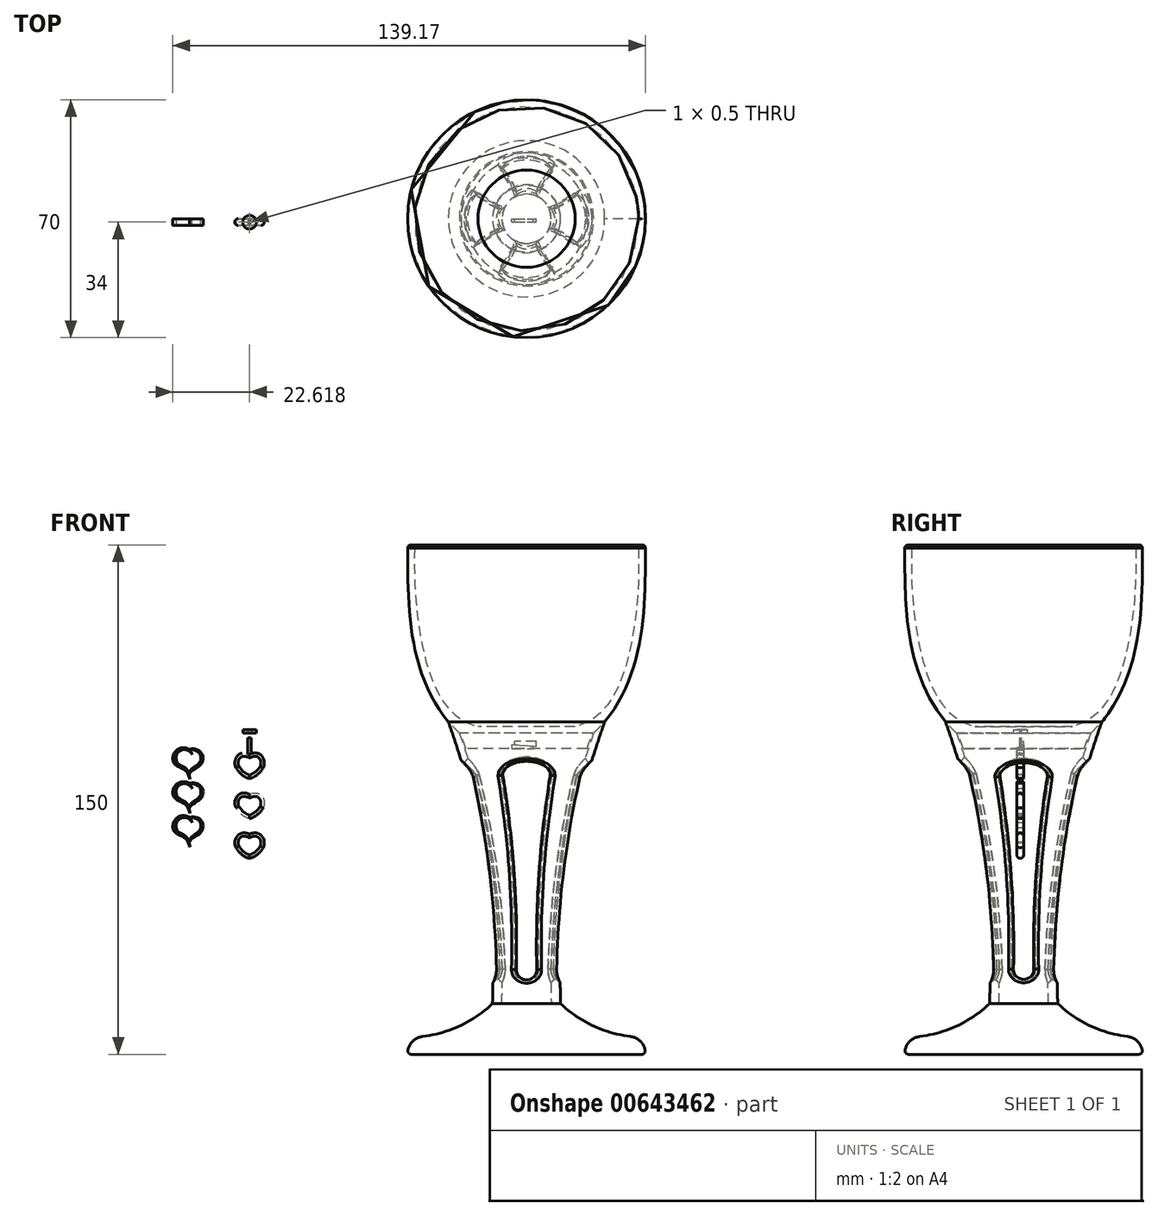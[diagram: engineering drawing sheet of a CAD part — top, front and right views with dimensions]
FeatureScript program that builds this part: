
annotation { "Feature Type Name" : "Feature", "Feature Type Description" : "" }
export const myFeature = defineFeature(function(context is Context, id is Id, definition is map)
    precondition{}
    {
        {
            var Q0;
            Q0=qCreatedBy(makeId("Front.planeOp"),FACE);
            var sketch = newSketch(context, id + "F0", { "sketchPlane" : qUnion([Q0])});
            skLineSegment(sketch, "E0", {"start": v(0, 130.44) * mm, "end": v(0, -127.8) * mm, "construction": true});
            skLineSegment(sketch, "E1", {"start": v(-47.74, 60) * mm, "end": v(50.5, 60) * mm, "construction": true});
            skLineSegment(sketch, "E2", {"start": v(-35, 85.65) * mm, "end": v(-35, -93.9) * mm, "construction": true});
            skFitSpline(sketch, "E3", {"points": [v(-33, 60) * mm, v(-33, 52.2) * mm, v(-31.65, 35.66) * mm, v(-19.66, 8.83) * mm, v(0, 5.37) * mm], "startDerivative": vector(0.17, -46.98) * mm, "endDerivative": vector(45.68, -2.23) * mm});
            skLineSegment(sketch, "E4", {"start": v(-35, 60) * mm, "end": v(-33, 60) * mm});
            skLineSegment(sketch, "E5", {"start": v(0, 5.37) * mm, "end": v(0, 0) * mm});
            skLineSegment(sketch, "E6.left", {"start": v(-35, -90) * mm, "end": v(-34.96, -85) * mm});
            skLineSegment(sketch, "E7", {"start": v(0, -75.08) * mm, "end": v(0, -90) * mm});
            skLineSegment(sketch, "E8", {"start": v(-35, -90) * mm, "end": v(0, -90) * mm});
            skLineSegment(sketch, "E9", {"start": v(-10.04, -75.08) * mm, "end": v(0, -75.08) * mm});
            skArc(sketch, "E10", {"start": v(-34.96, -85) * mm, "mid": v(-21.54, -82.44) * mm, "end": v(-10.04, -75.08) * mm});
            skArc(sketch, "E11", {"start": v(-10.04, -75.08) * mm, "mid": v(-12.53, -33) * mm, "end": v(-23, 7.81) * mm});
            skArc(sketch, "E12", {"start": v(-7.28, -75.08) * mm, "mid": v(-9.85, -34.66) * mm, "end": v(-19.78, 4.6) * mm});
            skLineSegment(sketch, "E13", {"start": v(0, -1.5) * mm, "end": v(0, -2.5) * mm});
            skLineSegment(sketch, "E14", {"start": v(61.71, 9.52) * mm, "end": v(61.71, -82.4) * mm, "construction": true});
            skLineSegment(sketch, "E15", {"start": v(56.71, 9.98) * mm, "end": v(56.71, -82.7) * mm, "construction": true});
            skLineSegment(sketch, "E16", {"start": v(66.71, 9.98) * mm, "end": v(66.71, -82.7) * mm, "construction": true});
            skCircle(sketch, "E17", {"center": v(61.71, -11.74) * mm, "radius": 5 * mm, "construction": true});
            skLineSegment(sketch, "E18", {"start": v(68.56, -11.74) * mm, "end": v(55.91, -11.74) * mm, "construction": true});
            skFitSpline(sketch, "E19", {"points": [v(56.71, -11.74) * mm, v(57.38, -9.69) * mm, v(58.5, -8.73) * mm, v(59.57, -8.36) * mm, v(60.79, -8.44) * mm, v(61.56, -8.81) * mm, v(62.29, -10.09) * mm], "startDerivative": vector(0, 9.46) * mm, "endDerivative": vector(1.96, -9.79) * mm});
            skFitSpline(sketch, "E20", {"points": [v(62.29, -10.09) * mm, v(61.51, -9.22) * mm, v(60.19, -8.85) * mm, v(58.82, -9.37) * mm, v(57.98, -10.52) * mm, v(57.77, -12.56) * mm, v(58.79, -14.06) * mm, v(60.05, -14.58) * mm, v(61.03, -15.06) * mm, v(61.7, -15.92) * mm, v(61.71, -16.74) * mm], "startDerivative": vector(-9, 11.38) * mm, "endDerivative": vector(1.36, -12.04) * mm});
            skFitSpline(sketch, "E21", {"points": [v(56.71, -11.74) * mm, v(57, -13.39) * mm, v(57.72, -14.57) * mm, v(58.7, -15.24) * mm, v(59.87, -15.43) * mm, v(60.66, -15.55) * mm, v(61.35, -16) * mm, v(61.71, -16.74) * mm], "startDerivative": vector(0.44, -8.79) * mm, "endDerivative": vector(1.87, -8.34) * mm});
            skFitSpline(sketch, "E22", {"points": [v(61.56, -8.81) * mm, v(62.83, -8.64) * mm, v(64.34, -9.22) * mm, v(65.25, -10.62) * mm, v(64.91, -12.42) * mm, v(63.93, -13.45) * mm, v(62.9, -14.12) * mm, v(62.02, -14.74) * mm, v(61.51, -15.54) * mm], "startDerivative": vector(10.18, 4.63) * mm, "endDerivative": vector(-2.51, -8.3) * mm});
            skFitSpline(sketch, "E23", {"points": [v(61.71, -8.96) * mm, v(62.62, -8.91) * mm, v(63.32, -9.16) * mm, v(63.92, -9.5) * mm, v(64.36, -10.01) * mm, v(64.59, -10.6) * mm, v(64.63, -11.56) * mm, v(64.27, -12.27) * mm, v(63.84, -12.76) * mm, v(63.38, -13.1) * mm, v(62.85, -13.48) * mm, v(62.33, -13.88) * mm, v(61.9, -14.3) * mm, v(61.53, -14.86) * mm, v(61.4, -15.4) * mm], "startDerivative": vector(9.48, 3.87) * mm, "endDerivative": vector(2.37, 8.87) * mm});
            skLineSegment(sketch, "E24", {"start": v(0, 0) * mm, "end": v(-17.82, 0) * mm});
            skLineSegment(sketch, "E25", {"start": v(-23, 7.81) * mm, "end": v(-19.78, 4.6) * mm});
            skFitSpline(sketch, "E26", {"points": [v(-35, 60) * mm, v(-23, 7.81) * mm], "startDerivative": vector(0, -56.24) * mm, "endDerivative": vector(36, -44.82) * mm});
            skLineSegment(sketch, "E27", {"start": v(-17.82, 0) * mm, "end": v(-19.37, 4.58) * mm});
            skLineSegment(sketch, "E28", {"start": v(-19.37, 4.58) * mm, "end": v(-19.78, 4.6) * mm});
            skLineSegment(sketch, "E29", {"start": v(-14.32, 6.5) * mm, "end": v(0, 6.5) * mm});
            skLineSegment(sketch, "E30", {"start": v(0, 6.5) * mm, "end": v(0, 5.37) * mm});
            skSolve(sketch);
        }
        {
            var Q0;
            Q0=makeQuery(id+"F0.imprint","IMPRINT",FACE,{"disambiguationData":[TD([[makeQuery(id+"F0.imprint","IMPRINT",EDGE,{"derivedFrom":sQuery(id+"F0.wireOp",EDGE,"E6.left")}),-1.0]])]});
            var Q1;
            {var subQ0=sQuery(id+"F0.wireOp",EDGE,"E11");Q1=makeQuery(id+"F0.imprint","IMPRINT",FACE,{"disambiguationData":[TD([[makeQuery(id+"F0.imprint","IMPRINT",EDGE,{"derivedFrom":subQ0}),-1.0]])]});}
            var Q2;
            Q2=sQuery(id+"F0.wireOp",EDGE,"E0");
            revolve(context, id + "F1", {"entities" : qUnion([Q0, Q1]), "axis" : qUnion([Q2]), "revolveType" : RevolveType.FULL});
        }
        {
            var Q0;
            Q0=makeQuery(id+"F0.imprint","IMPRINT",FACE,{"disambiguationData":[TD([[makeQuery(id+"F0.imprint","IMPRINT",EDGE,{"derivedFrom":sQuery(id+"F0.wireOp",EDGE,"E3")}),-1.0]])]});
            var Q1;
            {var subQ2=sQuery(id+"F0.wireOp",EDGE,"E29");Q1=makeQuery(id+"F0.imprint","IMPRINT",FACE,{"disambiguationData":[TD([[makeQuery(id+"F0.imprint","IMPRINT",EDGE,{"derivedFrom":subQ2}),-1.0]])]});}
            var Q2;
            Q2=sQuery(id+"F0.wireOp",EDGE,"E3");
            var Q3;
            Q3=sQuery(id+"F0.wireOp",EDGE,"58f8bd6e-e700-4917-940a-16b648b99986");
            var Q4;
            Q4=sQuery(id+"F0.wireOp",EDGE,"E4");
            var Q5;
            Q5=sQuery(id+"F0.wireOp",EDGE,"E0");
            revolve(context, id + "F2", {"entities" : qUnion([Q0, Q1]), "surfaceEntities" : qUnion([Q2, Q3, Q4]), "axis" : qUnion([Q5]), "revolveType" : RevolveType.FULL});
        }
        {
            var Q0;
            Q0=qCreatedBy(makeId("Front.planeOp"),FACE);
            var sketch = newSketch(context, id + "F3", { "sketchPlane" : qUnion([Q0])});
            skLineSegment(sketch, "E31", {"start": v(0, 0) * mm, "end": v(0, -71.87) * mm, "construction": true});
            skLineSegment(sketch, "E32", {"start": v(-19.04, -7.62) * mm, "end": v(33.65, -7.62) * mm, "construction": true});
            skLineSegment(sketch, "E33", {"start": v(-18.09, -65.08) * mm, "end": v(18.02, -65.08) * mm, "construction": true});
            skArc(sketch, "E34", {"start": v(-3, -65.08) * mm, "mid": v(-3.68, -36.26) * mm, "end": v(-7, -7.62) * mm});
            skArc(sketch, "E35", {"start": v(-3, -65.08) * mm, "mid": v(0, -68.08) * mm, "end": v(3, -65.08) * mm});
            skPoint(sketch, "E35.centerSnap0", {"position": v(-0.03, -65.08) * mm});
            skLineSegment(sketch, "E36", {"start": v(-7, -7.62) * mm, "end": v(0, -7.62) * mm});
            skLineSegment(sketch, "E37", {"start": v(0, -68.08) * mm, "end": v(0, -7.62) * mm});
            skArc(sketch, "E38.MirrorCS", {"start": v(3, -65.08) * mm, "mid": v(3.68, -36.26) * mm, "end": v(7, -7.62) * mm});
            skEllipse(sketch, "E39", {"center": v(0, -7.62) * mm, "majorRadius": 7 * mm, "minorRadius": 3.89 * mm, "majorAxis": v(-1, 0)});
            skSolve(sketch);
        }
        {
            var Q0;
            {var subQ6=sQuery(id+"F3.wireOp",EDGE,"E36");Q0=makeQuery(id+"F3.imprint","IMPRINT",FACE,{"disambiguationData":[TD([[makeQuery(id+"F3.imprint","IMPRINT",EDGE,{"derivedFrom":subQ6}),1.0]])]});}
            var Q1;
            {var subQ1=sQuery(id+"F3.wireOp",EDGE,"E36");Q1=makeQuery(id+"F3.imprint","IMPRINT",FACE,{"disambiguationData":[TD([[makeQuery(id+"F3.imprint","IMPRINT",EDGE,{"derivedFrom":subQ1}),-1.0]])]});}
            var Q2;
            {var subQ0=sQuery(id+"F3.wireOp",EDGE,"E35");var subQ1=sQuery(id+"F3.wireOp",EDGE,"E34");var subQ2=makeQuery(id+"F3.imprint","INTERSECT",VERTEX,{"derivedFrom":[subQ1,subQ0]});Q2=makeQuery(id+"F3.imprint","IMPRINT",FACE,{"disambiguationData":[TD([[makeQuery(id+"F3.imprint","IMPRINT",EDGE,{"disambiguationData":[TD([[subQ2,-1.0]])],"derivedFrom":subQ1}),-1.0]])]});}
            var Q3;
            {var subQ0=sQuery(id+"F3.wireOp",EDGE,"E38.MirrorCS");var subQ1=sQuery(id+"F3.wireOp",EDGE,"E35");var subQ2=makeQuery(id+"F3.imprint","INTERSECT",VERTEX,{"derivedFrom":[subQ1,subQ0]});Q3=makeQuery(id+"F3.imprint","IMPRINT",FACE,{"disambiguationData":[TD([[makeQuery(id+"F3.imprint","IMPRINT",EDGE,{"disambiguationData":[TD([[subQ2,1.0]])],"derivedFrom":subQ1}),1.0]])]});}
            extrude(context, id + "F4", {"entities" : qUnion([Q0, Q1, Q2, Q3]), "depth" : 50 * mm, "offsetDistance" : 25 * mm});
        }
        {
            var Q0;
            Q0=makeQuery(id+"F4.opExtrude","SWEPT_BODY",BODY,{"disambiguationData":[OSD([sQuery(id+"F3.wireOp",EDGE,"E34"),sQuery(id+"F3.wireOp",EDGE,"E35"),sQuery(id+"F3.wireOp",EDGE,"E38.MirrorCS"),sQuery(id+"F3.wireOp",EDGE,"E39")])]});
            transform(context, id + "F5", {"entities" : qUnion([Q0]), "transformType" : TransformType.TRANSLATION_3D, "dx" : 0 * mm, "dy" : 25 * mm, "dz" : 0 * mm, "makeCopy" : false});
        }
        {
            var Q0;
            Q0=makeQuery(id+"F4.opExtrude","SWEPT_BODY",BODY,{"disambiguationData":[OSD([sQuery(id+"F3.wireOp",EDGE,"E34"),sQuery(id+"F3.wireOp",EDGE,"E35"),sQuery(id+"F3.wireOp",EDGE,"E38.MirrorCS"),sQuery(id+"F3.wireOp",EDGE,"E39")])]});
            var Q1;
            Q1=makeQuery(id+"F1.opRevolve","SWEPT_BODY",BODY,{"disambiguationData":[OSD([sQuery(id+"F0.wireOp",EDGE,"58f8bd6e-e700-4917-940a-16b648b99986"),sQuery(id+"F0.wireOp",EDGE,"E3"),sQuery(id+"F0.wireOp",EDGE,"E4"),sQuery(id+"F0.wireOp",EDGE,"E5"),sQuery(id+"F0.wireOp",EDGE,"E6.left"),sQuery(id+"F0.wireOp",EDGE,"E7"),sQuery(id+"F0.wireOp",EDGE,"E8"),sQuery(id+"F0.wireOp",EDGE,"E9"),sQuery(id+"F0.wireOp",EDGE,"E10"),sQuery(id+"F0.wireOp",EDGE,"E11"),sQuery(id+"F0.wireOp",EDGE,"E12")])]});
            booleanBodies(context, id + "F6", {"operationType" : BooleanOperationType.SUBTRACTION, "tools" : qUnion([Q0]), "targets" : qUnion([Q1])});
        }
        {
            var Q0;
            Q0=qCreatedBy(makeId("Right.planeOp"),FACE);
            var sketch = newSketch(context, id + "F7", { "sketchPlane" : qUnion([Q0])});
            skLineSegment(sketch, "E40", {"start": v(0, -0.03) * mm, "end": v(0, -71.9) * mm, "construction": true});
            skLineSegment(sketch, "E41", {"start": v(-16.9, -8.05) * mm, "end": v(35.8, -8.05) * mm, "construction": true});
            skLineSegment(sketch, "E42", {"start": v(-14.28, -64.93) * mm, "end": v(21.82, -64.93) * mm, "construction": true});
            skArc(sketch, "E43", {"start": v(-3, -64.93) * mm, "mid": v(-3.7, -36.4) * mm, "end": v(-7, -8.05) * mm});
            skArc(sketch, "E44", {"start": v(-3, -64.93) * mm, "mid": v(0, -67.93) * mm, "end": v(3, -64.93) * mm});
            skPoint(sketch, "E44.centerSnap0", {"position": v(3.77, -64.93) * mm});
            skLineSegment(sketch, "E45", {"start": v(-7, -8.05) * mm, "end": v(0, -8.05) * mm});
            skLineSegment(sketch, "E46", {"start": v(0, -67.93) * mm, "end": v(0, -8.05) * mm});
            skArc(sketch, "E47.MirrorCS", {"start": v(3, -64.93) * mm, "mid": v(3.7, -36.4) * mm, "end": v(7, -8.05) * mm});
            skEllipse(sketch, "E48", {"center": v(0, -8.05) * mm, "majorRadius": 7 * mm, "minorRadius": 3.89 * mm, "majorAxis": v(-1, 0)});
            skSolve(sketch);
        }
        {
            var Q0;
            {var subQ6=sQuery(id+"F7.wireOp",EDGE,"E45");Q0=makeQuery(id+"F7.imprint","IMPRINT",FACE,{"disambiguationData":[TD([[makeQuery(id+"F7.imprint","IMPRINT",EDGE,{"derivedFrom":subQ6}),1.0]])]});}
            var Q1;
            {var subQ1=sQuery(id+"F7.wireOp",EDGE,"E45");Q1=makeQuery(id+"F7.imprint","IMPRINT",FACE,{"disambiguationData":[TD([[makeQuery(id+"F7.imprint","IMPRINT",EDGE,{"derivedFrom":subQ1}),-1.0]])]});}
            var Q2;
            {var subQ0=sQuery(id+"F7.wireOp",EDGE,"E44");var subQ1=sQuery(id+"F7.wireOp",EDGE,"E43");var subQ2=makeQuery(id+"F7.imprint","INTERSECT",VERTEX,{"derivedFrom":[subQ1,subQ0]});Q2=makeQuery(id+"F7.imprint","IMPRINT",FACE,{"disambiguationData":[TD([[makeQuery(id+"F7.imprint","IMPRINT",EDGE,{"disambiguationData":[TD([[subQ2,-1.0]])],"derivedFrom":subQ1}),-1.0]])]});}
            var Q3;
            {var subQ0=sQuery(id+"F7.wireOp",EDGE,"E47.MirrorCS");var subQ1=sQuery(id+"F7.wireOp",EDGE,"E44");var subQ2=makeQuery(id+"F7.imprint","INTERSECT",VERTEX,{"derivedFrom":[subQ1,subQ0]});Q3=makeQuery(id+"F7.imprint","IMPRINT",FACE,{"disambiguationData":[TD([[makeQuery(id+"F7.imprint","IMPRINT",EDGE,{"disambiguationData":[TD([[subQ2,1.0]])],"derivedFrom":subQ1}),1.0]])]});}
            extrude(context, id + "F8", {"entities" : qUnion([Q0, Q1, Q2, Q3]), "depth" : 50 * mm, "offsetDistance" : 25 * mm});
        }
        {
            var Q0;
            Q0=makeQuery(id+"F8.opExtrude","SWEPT_BODY",BODY,{"disambiguationData":[OSD([sQuery(id+"F7.wireOp",EDGE,"E43"),sQuery(id+"F7.wireOp",EDGE,"E44"),sQuery(id+"F7.wireOp",EDGE,"E47.MirrorCS"),sQuery(id+"F7.wireOp",EDGE,"E48")])]});
            transform(context, id + "F9", {"entities" : qUnion([Q0]), "transformType" : TransformType.TRANSLATION_3D, "dx" : -25 * mm, "dy" : 0 * mm, "dz" : 0 * mm, "makeCopy" : false});
        }
        {
            var Q0;
            Q0=makeQuery(id+"F8.opExtrude","SWEPT_BODY",BODY,{"disambiguationData":[OSD([sQuery(id+"F7.wireOp",EDGE,"E43"),sQuery(id+"F7.wireOp",EDGE,"E44"),sQuery(id+"F7.wireOp",EDGE,"E47.MirrorCS"),sQuery(id+"F7.wireOp",EDGE,"E48")])]});
            var Q1;
            Q1=makeQuery(id+"F1.opRevolve","SWEPT_BODY",BODY,{"disambiguationData":[OSD([sQuery(id+"F0.wireOp",EDGE,"58f8bd6e-e700-4917-940a-16b648b99986"),sQuery(id+"F0.wireOp",EDGE,"E6.left"),sQuery(id+"F0.wireOp",EDGE,"E7"),sQuery(id+"F0.wireOp",EDGE,"E8"),sQuery(id+"F0.wireOp",EDGE,"E9"),sQuery(id+"F0.wireOp",EDGE,"E10"),sQuery(id+"F0.wireOp",EDGE,"E11"),sQuery(id+"F0.wireOp",EDGE,"E12")])]});
            booleanBodies(context, id + "F10", {"operationType" : BooleanOperationType.SUBTRACTION, "tools" : qUnion([Q0]), "targets" : qUnion([Q1])});
        }
        {
            var Q0;
            Q0=makeQuery(id+"F1.opRevolve","SWEPT_EDGE",EDGE,{"disambiguationData":[OSD([sQuery(id+"F0.wireOp",EDGE,"E6.left"),sQuery(id+"F0.wireOp",EDGE,"E10")])]});
            fillet(context, id + "F11", {"entities" : qUnion([Q0]), "radius" : 5 * mm, "tangentPropagation" : true, "allowEdgeOverflow" : false});
        }
        {
            var Q0;
            Q0=makeQuery(id+"F1.opRevolve","SWEPT_EDGE",EDGE,{"disambiguationData":[OSD([sQuery(id+"F0.wireOp",EDGE,"E6.left"),sQuery(id+"F0.wireOp",EDGE,"E8")])]});
            fillet(context, id + "F12", {"entities" : qUnion([Q0]), "radius" : 1 * mm, "tangentPropagation" : true, "allowEdgeOverflow" : false});
        }
        {
            var Q0;
            Q0=makeQuery(id+"F10.opBoolean","INTERSECT",EDGE,{"disambiguationData":[OD(1.0)],"derivedFrom":[makeQuery(id+"F1.opRevolve","SWEPT_FACE",FACE,{"disambiguationData":[OSD([sQuery(id+"F0.wireOp",EDGE,"E11")])]}),makeQuery(id+"F8.opExtrude","SWEPT_FACE",FACE,{"disambiguationData":[OSD([sQuery(id+"F7.wireOp",EDGE,"E47.MirrorCS")])]})]});
            var Q1;
            Q1=makeQuery(id+"F10.opBoolean","INTERSECT",EDGE,{"disambiguationData":[OD(1.0)],"derivedFrom":[makeQuery(id+"F1.opRevolve","SWEPT_FACE",FACE,{"disambiguationData":[OSD([sQuery(id+"F0.wireOp",EDGE,"E11")])]}),makeQuery(id+"F8.opExtrude","SWEPT_FACE",FACE,{"disambiguationData":[OSD([sQuery(id+"F7.wireOp",EDGE,"E48")])]})]});
            var Q2;
            Q2=makeQuery(id+"F10.opBoolean","INTERSECT",EDGE,{"disambiguationData":[OD(1.0)],"derivedFrom":[makeQuery(id+"F1.opRevolve","SWEPT_FACE",FACE,{"disambiguationData":[OSD([sQuery(id+"F0.wireOp",EDGE,"E11")])]}),makeQuery(id+"F8.opExtrude","SWEPT_FACE",FACE,{"disambiguationData":[OSD([sQuery(id+"F7.wireOp",EDGE,"E43")])]})]});
            var Q3;
            Q3=makeQuery(id+"F6.opBoolean","INTERSECT",EDGE,{"disambiguationData":[OD(1.0)],"derivedFrom":[makeQuery(id+"F1.opRevolve","SWEPT_FACE",FACE,{"disambiguationData":[OSD([sQuery(id+"F0.wireOp",EDGE,"E11")])]}),makeQuery(id+"F4.opExtrude","SWEPT_FACE",FACE,{"disambiguationData":[OSD([sQuery(id+"F3.wireOp",EDGE,"E34")])]})]});
            var Q4;
            Q4=makeQuery(id+"F6.opBoolean","INTERSECT",EDGE,{"disambiguationData":[OD(1.0)],"derivedFrom":[makeQuery(id+"F1.opRevolve","SWEPT_FACE",FACE,{"disambiguationData":[OSD([sQuery(id+"F0.wireOp",EDGE,"E11")])]}),makeQuery(id+"F4.opExtrude","SWEPT_FACE",FACE,{"disambiguationData":[OSD([sQuery(id+"F3.wireOp",EDGE,"E35")])]})]});
            var Q5;
            Q5=makeQuery(id+"F6.opBoolean","INTERSECT",EDGE,{"disambiguationData":[OD(1.0)],"derivedFrom":[makeQuery(id+"F1.opRevolve","SWEPT_FACE",FACE,{"disambiguationData":[OSD([sQuery(id+"F0.wireOp",EDGE,"E11")])]}),makeQuery(id+"F4.opExtrude","SWEPT_FACE",FACE,{"disambiguationData":[OSD([sQuery(id+"F3.wireOp",EDGE,"E38.MirrorCS")])]})]});
            var Q6;
            Q6=makeQuery(id+"F6.opBoolean","INTERSECT",EDGE,{"disambiguationData":[OD(1.0)],"derivedFrom":[makeQuery(id+"F1.opRevolve","SWEPT_FACE",FACE,{"disambiguationData":[OSD([sQuery(id+"F0.wireOp",EDGE,"E11")])]}),makeQuery(id+"F4.opExtrude","SWEPT_FACE",FACE,{"disambiguationData":[OSD([sQuery(id+"F3.wireOp",EDGE,"E39")])]})]});
            var Q7;
            Q7=makeQuery(id+"F6.opBoolean","INTERSECT",EDGE,{"disambiguationData":[OD(1.0)],"derivedFrom":[makeQuery(id+"F1.opRevolve","SWEPT_FACE",FACE,{"disambiguationData":[OSD([sQuery(id+"F0.wireOp",EDGE,"E12")])]}),makeQuery(id+"F4.opExtrude","SWEPT_FACE",FACE,{"disambiguationData":[OSD([sQuery(id+"F3.wireOp",EDGE,"E39")])]})]});
            var Q8;
            Q8=makeQuery(id+"F6.opBoolean","INTERSECT",EDGE,{"disambiguationData":[OD(1.0)],"derivedFrom":[makeQuery(id+"F1.opRevolve","SWEPT_FACE",FACE,{"disambiguationData":[OSD([sQuery(id+"F0.wireOp",EDGE,"E12")])]}),makeQuery(id+"F4.opExtrude","SWEPT_FACE",FACE,{"disambiguationData":[OSD([sQuery(id+"F3.wireOp",EDGE,"E34")])]})]});
            var Q9;
            Q9=makeQuery(id+"F6.opBoolean","INTERSECT",EDGE,{"disambiguationData":[OD(1.0)],"derivedFrom":[makeQuery(id+"F1.opRevolve","SWEPT_FACE",FACE,{"disambiguationData":[OSD([sQuery(id+"F0.wireOp",EDGE,"E12")])]}),makeQuery(id+"F4.opExtrude","SWEPT_FACE",FACE,{"disambiguationData":[OSD([sQuery(id+"F3.wireOp",EDGE,"E35")])]})]});
            var Q10;
            Q10=makeQuery(id+"F6.opBoolean","INTERSECT",EDGE,{"disambiguationData":[OD(1.0)],"derivedFrom":[makeQuery(id+"F1.opRevolve","SWEPT_FACE",FACE,{"disambiguationData":[OSD([sQuery(id+"F0.wireOp",EDGE,"E12")])]}),makeQuery(id+"F4.opExtrude","SWEPT_FACE",FACE,{"disambiguationData":[OSD([sQuery(id+"F3.wireOp",EDGE,"E38.MirrorCS")])]})]});
            var Q11;
            Q11=makeQuery(id+"F10.opBoolean","INTERSECT",EDGE,{"disambiguationData":[OD(1.0)],"derivedFrom":[makeQuery(id+"F1.opRevolve","SWEPT_FACE",FACE,{"disambiguationData":[OSD([sQuery(id+"F0.wireOp",EDGE,"E12")])]}),makeQuery(id+"F8.opExtrude","SWEPT_FACE",FACE,{"disambiguationData":[OSD([sQuery(id+"F7.wireOp",EDGE,"E43")])]})]});
            var Q12;
            Q12=makeQuery(id+"F10.opBoolean","INTERSECT",EDGE,{"disambiguationData":[OD(1.0)],"derivedFrom":[makeQuery(id+"F1.opRevolve","SWEPT_FACE",FACE,{"disambiguationData":[OSD([sQuery(id+"F0.wireOp",EDGE,"E12")])]}),makeQuery(id+"F8.opExtrude","SWEPT_FACE",FACE,{"disambiguationData":[OSD([sQuery(id+"F7.wireOp",EDGE,"E44")])]})]});
            var Q13;
            Q13=makeQuery(id+"F10.opBoolean","INTERSECT",EDGE,{"disambiguationData":[OD(1.0)],"derivedFrom":[makeQuery(id+"F1.opRevolve","SWEPT_FACE",FACE,{"disambiguationData":[OSD([sQuery(id+"F0.wireOp",EDGE,"E12")])]}),makeQuery(id+"F8.opExtrude","SWEPT_FACE",FACE,{"disambiguationData":[OSD([sQuery(id+"F7.wireOp",EDGE,"E47.MirrorCS")])]})]});
            var Q14;
            Q14=makeQuery(id+"F10.opBoolean","INTERSECT",EDGE,{"disambiguationData":[OD(1.0)],"derivedFrom":[makeQuery(id+"F1.opRevolve","SWEPT_FACE",FACE,{"disambiguationData":[OSD([sQuery(id+"F0.wireOp",EDGE,"E12")])]}),makeQuery(id+"F8.opExtrude","SWEPT_FACE",FACE,{"disambiguationData":[OSD([sQuery(id+"F7.wireOp",EDGE,"E48")])]})]});
            var Q15;
            Q15=makeQuery(id+"F6.opBoolean","INTERSECT",EDGE,{"disambiguationData":[OD(0.0)],"derivedFrom":[makeQuery(id+"F1.opRevolve","SWEPT_FACE",FACE,{"disambiguationData":[OSD([sQuery(id+"F0.wireOp",EDGE,"E12")])]}),makeQuery(id+"F4.opExtrude","SWEPT_FACE",FACE,{"disambiguationData":[OSD([sQuery(id+"F3.wireOp",EDGE,"E38.MirrorCS")])]})]});
            var Q16;
            Q16=makeQuery(id+"F6.opBoolean","INTERSECT",EDGE,{"disambiguationData":[OD(0.0)],"derivedFrom":[makeQuery(id+"F1.opRevolve","SWEPT_FACE",FACE,{"disambiguationData":[OSD([sQuery(id+"F0.wireOp",EDGE,"E12")])]}),makeQuery(id+"F4.opExtrude","SWEPT_FACE",FACE,{"disambiguationData":[OSD([sQuery(id+"F3.wireOp",EDGE,"E39")])]})]});
            var Q17;
            Q17=makeQuery(id+"F6.opBoolean","INTERSECT",EDGE,{"disambiguationData":[OD(0.0)],"derivedFrom":[makeQuery(id+"F1.opRevolve","SWEPT_FACE",FACE,{"disambiguationData":[OSD([sQuery(id+"F0.wireOp",EDGE,"E12")])]}),makeQuery(id+"F4.opExtrude","SWEPT_FACE",FACE,{"disambiguationData":[OSD([sQuery(id+"F3.wireOp",EDGE,"E34")])]})]});
            var Q18;
            Q18=makeQuery(id+"F6.opBoolean","INTERSECT",EDGE,{"disambiguationData":[OD(0.0)],"derivedFrom":[makeQuery(id+"F1.opRevolve","SWEPT_FACE",FACE,{"disambiguationData":[OSD([sQuery(id+"F0.wireOp",EDGE,"E12")])]}),makeQuery(id+"F4.opExtrude","SWEPT_FACE",FACE,{"disambiguationData":[OSD([sQuery(id+"F3.wireOp",EDGE,"E35")])]})]});
            var Q19;
            Q19=makeQuery(id+"F6.opBoolean","INTERSECT",EDGE,{"disambiguationData":[OD(0.0)],"derivedFrom":[makeQuery(id+"F1.opRevolve","SWEPT_FACE",FACE,{"disambiguationData":[OSD([sQuery(id+"F0.wireOp",EDGE,"E11")])]}),makeQuery(id+"F4.opExtrude","SWEPT_FACE",FACE,{"disambiguationData":[OSD([sQuery(id+"F3.wireOp",EDGE,"E35")])]})]});
            var Q20;
            Q20=makeQuery(id+"F6.opBoolean","INTERSECT",EDGE,{"disambiguationData":[OD(0.0)],"derivedFrom":[makeQuery(id+"F1.opRevolve","SWEPT_FACE",FACE,{"disambiguationData":[OSD([sQuery(id+"F0.wireOp",EDGE,"E11")])]}),makeQuery(id+"F4.opExtrude","SWEPT_FACE",FACE,{"disambiguationData":[OSD([sQuery(id+"F3.wireOp",EDGE,"E38.MirrorCS")])]})]});
            var Q21;
            Q21=makeQuery(id+"F6.opBoolean","INTERSECT",EDGE,{"disambiguationData":[OD(0.0)],"derivedFrom":[makeQuery(id+"F1.opRevolve","SWEPT_FACE",FACE,{"disambiguationData":[OSD([sQuery(id+"F0.wireOp",EDGE,"E11")])]}),makeQuery(id+"F4.opExtrude","SWEPT_FACE",FACE,{"disambiguationData":[OSD([sQuery(id+"F3.wireOp",EDGE,"E39")])]})]});
            var Q22;
            Q22=makeQuery(id+"F6.opBoolean","INTERSECT",EDGE,{"disambiguationData":[OD(0.0)],"derivedFrom":[makeQuery(id+"F1.opRevolve","SWEPT_FACE",FACE,{"disambiguationData":[OSD([sQuery(id+"F0.wireOp",EDGE,"E11")])]}),makeQuery(id+"F4.opExtrude","SWEPT_FACE",FACE,{"disambiguationData":[OSD([sQuery(id+"F3.wireOp",EDGE,"E34")])]})]});
            var Q23;
            Q23=makeQuery(id+"F10.opBoolean","INTERSECT",EDGE,{"disambiguationData":[OD(0.0)],"derivedFrom":[makeQuery(id+"F1.opRevolve","SWEPT_FACE",FACE,{"disambiguationData":[OSD([sQuery(id+"F0.wireOp",EDGE,"E11")])]}),makeQuery(id+"F8.opExtrude","SWEPT_FACE",FACE,{"disambiguationData":[OSD([sQuery(id+"F7.wireOp",EDGE,"E48")])]})]});
            var Q24;
            Q24=makeQuery(id+"F10.opBoolean","INTERSECT",EDGE,{"disambiguationData":[OD(0.0)],"derivedFrom":[makeQuery(id+"F1.opRevolve","SWEPT_FACE",FACE,{"disambiguationData":[OSD([sQuery(id+"F0.wireOp",EDGE,"E11")])]}),makeQuery(id+"F8.opExtrude","SWEPT_FACE",FACE,{"disambiguationData":[OSD([sQuery(id+"F7.wireOp",EDGE,"E43")])]})]});
            var Q25;
            Q25=makeQuery(id+"F10.opBoolean","INTERSECT",EDGE,{"disambiguationData":[OD(0.0)],"derivedFrom":[makeQuery(id+"F1.opRevolve","SWEPT_FACE",FACE,{"disambiguationData":[OSD([sQuery(id+"F0.wireOp",EDGE,"E11")])]}),makeQuery(id+"F8.opExtrude","SWEPT_FACE",FACE,{"disambiguationData":[OSD([sQuery(id+"F7.wireOp",EDGE,"E47.MirrorCS")])]})]});
            var Q26;
            Q26=makeQuery(id+"F10.opBoolean","INTERSECT",EDGE,{"disambiguationData":[OD(0.0)],"derivedFrom":[makeQuery(id+"F1.opRevolve","SWEPT_FACE",FACE,{"disambiguationData":[OSD([sQuery(id+"F0.wireOp",EDGE,"E12")])]}),makeQuery(id+"F8.opExtrude","SWEPT_FACE",FACE,{"disambiguationData":[OSD([sQuery(id+"F7.wireOp",EDGE,"E47.MirrorCS")])]})]});
            var Q27;
            Q27=makeQuery(id+"F10.opBoolean","INTERSECT",EDGE,{"disambiguationData":[OD(0.0)],"derivedFrom":[makeQuery(id+"F1.opRevolve","SWEPT_FACE",FACE,{"disambiguationData":[OSD([sQuery(id+"F0.wireOp",EDGE,"E12")])]}),makeQuery(id+"F8.opExtrude","SWEPT_FACE",FACE,{"disambiguationData":[OSD([sQuery(id+"F7.wireOp",EDGE,"E48")])]})]});
            var Q28;
            Q28=makeQuery(id+"F10.opBoolean","INTERSECT",EDGE,{"disambiguationData":[OD(0.0)],"derivedFrom":[makeQuery(id+"F1.opRevolve","SWEPT_FACE",FACE,{"disambiguationData":[OSD([sQuery(id+"F0.wireOp",EDGE,"E12")])]}),makeQuery(id+"F8.opExtrude","SWEPT_FACE",FACE,{"disambiguationData":[OSD([sQuery(id+"F7.wireOp",EDGE,"E43")])]})]});
            chamfer(context, id + "F13", {"entities" : qUnion([Q0, Q1, Q2, Q3, Q4, Q5, Q6, Q7, Q8, Q9, Q10, Q11, Q12, Q13, Q14, Q15, Q16, Q17, Q18, Q19, Q20, Q21, Q22, Q23, Q24, Q25, Q26, Q27, Q28]), "width" : 1 * mm, "tangentPropagation" : true});
        }
        {
            var Q0;
            Q0=qCreatedBy(makeId("Front.planeOp"),FACE);
            var sketch = newSketch(context, id + "F14", { "sketchPlane" : qUnion([Q0])});
            skFitSpline(sketch, "E49", {"points": [v(-104.16, -3.27) * mm, v(-103.81, -1.43) * mm, v(-102.82, -0.3) * mm, v(-101.49, 0.25) * mm, v(-100.15, 0.16) * mm, v(-99.3, -0.26) * mm, v(-98.5, -1.66) * mm], "startDerivative": vector(-0.83, 11.2) * mm, "endDerivative": vector(2.18, -10.8) * mm});
            skFitSpline(sketch, "E50", {"points": [v(-98.5, -1.66) * mm, v(-99.33, -0.7) * mm, v(-100.8, -0.3) * mm, v(-102.31, -0.87) * mm, v(-103.2, -2.41) * mm, v(-102.76, -4.2) * mm, v(-101.49, -5.09) * mm, v(-100.32, -5.78) * mm, v(-99.64, -6.78) * mm, v(-99.21, -8.14) * mm, v(-99.1, -9.01) * mm], "startDerivative": vector(-9.93, 12.58) * mm, "endDerivative": vector(1.3, -13.21) * mm});
            skFitSpline(sketch, "E51", {"points": [v(-104.16, -3.27) * mm, v(-103.44, -4.7) * mm, v(-102.32, -5.44) * mm, v(-101.3, -5.92) * mm, v(-100.46, -6.42) * mm, v(-99.88, -7.08) * mm, v(-99.48, -7.96) * mm, v(-99.1, -9.01) * mm], "startDerivative": vector(0.07, -9.72) * mm, "endDerivative": vector(2.07, -9.2) * mm});
            skFitSpline(sketch, "E52", {"points": [v(-99.3, -0.26) * mm, v(-97.88, -0.06) * mm, v(-96.22, -0.7) * mm, v(-95.21, -2.25) * mm, v(-95.59, -4.23) * mm, v(-96.67, -5.38) * mm, v(-97.8, -6.11) * mm, v(-98.79, -6.8) * mm, v(-99.33, -7.67) * mm], "startDerivative": vector(11.25, 5.1) * mm, "endDerivative": vector(-2.78, -9.18) * mm});
            skFitSpline(sketch, "E53", {"points": [v(-99.12, -0.42) * mm, v(-98.13, -0.36) * mm, v(-97.34, -0.63) * mm, v(-96.68, -1) * mm, v(-96.2, -1.58) * mm, v(-95.95, -2.24) * mm, v(-95.9, -3.29) * mm, v(-96.3, -4.07) * mm, v(-96.77, -4.61) * mm, v(-97.28, -4.99) * mm, v(-97.87, -5.4) * mm, v(-98.44, -5.86) * mm, v(-98.92, -6.3) * mm, v(-99.33, -6.94) * mm, v(-99.38, -7.5) * mm], "startDerivative": vector(10.46, 4.3) * mm, "endDerivative": vector(-0.03, -4.32) * mm});
            skLineSegment(sketch, "E54", {"start": v(-81.55, 5.95) * mm, "end": v(-81.55, -28.95) * mm, "construction": true});
            skLineSegment(sketch, "E55", {"start": v(-85.55, 6.21) * mm, "end": v(-85.55, -28.95) * mm, "construction": true});
            skLineSegment(sketch, "E56", {"start": v(-77.55, 5.76) * mm, "end": v(-77.55, -28.95) * mm, "construction": true});
            skCircle(sketch, "E57", {"center": v(-81.55, -5.64) * mm, "radius": 4 * mm, "construction": true});
            skLineSegment(sketch, "E58", {"start": v(-86.46, -5.64) * mm, "end": v(-76.86, -5.64) * mm, "construction": true});
            skFitSpline(sketch, "E59", {"points": [v(-85.55, -5.64) * mm, v(-81.55, -1.64) * mm], "startDerivative": vector(-3.42, 6.6) * mm, "endDerivative": vector(10.02, -4.5) * mm});
            skFitSpline(sketch, "E60.MirrorCS", {"points": [v(-77.55, -5.64) * mm, v(-81.55, -1.64) * mm], "startDerivative": vector(3.42, 6.6) * mm, "endDerivative": vector(-10.02, -4.5) * mm});
            skFitSpline(sketch, "E61", {"points": [v(-85.55, -5.64) * mm, v(-81.55, -8.8) * mm], "startDerivative": vector(2.76, -4.72) * mm, "endDerivative": vector(4.74, -1) * mm});
            skFitSpline(sketch, "E62", {"points": [v(-77.55, -5.64) * mm, v(-81.55, -8.8) * mm], "startDerivative": vector(-2.41, -4.72) * mm, "endDerivative": vector(-4.3, -1) * mm});
            skLineSegment(sketch, "E63", {"start": v(-74.95, 0) * mm, "end": v(-87.26, 0) * mm, "construction": true});
            skLineSegment(sketch, "E64.bottom", {"start": v(-82.05, 3.65) * mm, "end": v(-81.05, 3.65) * mm});
            skLineSegment(sketch, "E64.top", {"start": v(-82.05, -1.35) * mm, "end": v(-81.05, -1.35) * mm});
            skLineSegment(sketch, "E64.left", {"start": v(-82.05, 3.65) * mm, "end": v(-82.05, -1.35) * mm});
            skLineSegment(sketch, "E64.right", {"start": v(-81.05, 3.65) * mm, "end": v(-81.05, -1.35) * mm});
            skSolve(sketch);
        }
        {
            var Q0;
            {var subQ8=sQuery(id+"F14.wireOp",EDGE,"E51");Q0=makeQuery(id+"F14.imprint","IMPRINT",FACE,{"disambiguationData":[TD([[makeQuery(id+"F14.imprint","IMPRINT",EDGE,{"derivedFrom":subQ8}),1.0]])]});}
            var Q1;
            {var subQ0=sQuery(id+"F14.wireOp",EDGE,"E52");Q1=makeQuery(id+"F14.imprint","IMPRINT",FACE,{"disambiguationData":[TD([[makeQuery(id+"F14.imprint","IMPRINT",EDGE,{"derivedFrom":subQ0}),-1.0]])]});}
            extrude(context, id + "F15", {"entities" : qUnion([Q0, Q1]), "depth" : 2 * mm, "offsetDistance" : 25 * mm});
        }
        {
            var Q0;
            {var subQ0=sQuery(id+"F14.wireOp",EDGE,"E49");Q0=makeQuery(id+"F15.opExtrude","CAP_EDGE",EDGE,{"disambiguationData":[OSD([subQ0]),TDD([makeQuery(id+"F14.imprint","IMPRINT",EDGE,{"disambiguationData":[TD([[makeQuery(id+"F14.imprint","INTERSECT",VERTEX,{"derivedFrom":[subQ0,sQuery(id+"F14.wireOp",EDGE,"E51")]}),-1.0]])],"derivedFrom":subQ0})])],"isStart":false});}
            var Q1;
            {var subQ0=sQuery(id+"F14.wireOp",EDGE,"E50");Q1=makeQuery(id+"F15.opExtrude","CAP_EDGE",EDGE,{"disambiguationData":[OSD([subQ0]),TDD([makeQuery(id+"F14.imprint","IMPRINT",EDGE,{"disambiguationData":[TD([[makeQuery(id+"F14.imprint","INTERSECT",VERTEX,{"derivedFrom":[sQuery(id+"F14.wireOp",EDGE,"E49"),subQ0]}),-1.0]])],"derivedFrom":subQ0})])],"isStart":false});}
            var Q2;
            Q2=makeQuery(id+"F15.opExtrude","CAP_EDGE",EDGE,{"disambiguationData":[OSD([sQuery(id+"F14.wireOp",EDGE,"E51")])],"isStart":false});
            var Q3;
            {var subQ0=sQuery(id+"F14.wireOp",EDGE,"E49");Q3=makeQuery(id+"F15.opExtrude","CAP_EDGE",EDGE,{"disambiguationData":[OSD([subQ0]),TDD([makeQuery(id+"F14.imprint","IMPRINT",EDGE,{"disambiguationData":[TD([[makeQuery(id+"F14.imprint","INTERSECT",VERTEX,{"derivedFrom":[subQ0,sQuery(id+"F14.wireOp",EDGE,"E51")]}),-1.0]])],"derivedFrom":subQ0})])],"isStart":true});}
            var Q4;
            {var subQ0=sQuery(id+"F14.wireOp",EDGE,"E50");Q4=makeQuery(id+"F15.opExtrude","CAP_EDGE",EDGE,{"disambiguationData":[OSD([subQ0]),TDD([makeQuery(id+"F14.imprint","IMPRINT",EDGE,{"disambiguationData":[TD([[makeQuery(id+"F14.imprint","INTERSECT",VERTEX,{"derivedFrom":[sQuery(id+"F14.wireOp",EDGE,"E49"),subQ0]}),-1.0]])],"derivedFrom":subQ0})])],"isStart":true});}
            var Q5;
            Q5=makeQuery(id+"F15.opExtrude","CAP_EDGE",EDGE,{"disambiguationData":[OSD([sQuery(id+"F14.wireOp",EDGE,"E51")])],"isStart":true});
            fillet(context, id + "F16", {"entities" : qUnion([Q0, Q1, Q2, Q3, Q4, Q5]), "radius" : 0.2 * mm, "tangentPropagation" : true, "allowEdgeOverflow" : false});
        }
        {
            var Q0;
            Q0=makeQuery(id+"F15.opExtrude","SWEPT_BODY",BODY,{"disambiguationData":[OSD([sQuery(id+"F14.wireOp",EDGE,"E49"),sQuery(id+"F14.wireOp",EDGE,"E50"),sQuery(id+"F14.wireOp",EDGE,"E51"),sQuery(id+"F14.wireOp",EDGE,"E52"),sQuery(id+"F14.wireOp",EDGE,"E53")])]});
            transform(context, id + "F17", {"entities" : qUnion([Q0]), "transformType" : TransformType.TRANSLATION_3D, "dx" : 0 * mm, "dy" : 0 * mm, "dz" : -10 * mm, "makeCopy" : true});
        }
        {
            var Q0;
            Q0=makeQuery(id+"F17.opPattern","COPY",BODY,{"derivedFrom":makeQuery(id+"F15.opExtrude","SWEPT_BODY",BODY,{"disambiguationData":[OSD([sQuery(id+"F14.wireOp",EDGE,"E49"),sQuery(id+"F14.wireOp",EDGE,"E50"),sQuery(id+"F14.wireOp",EDGE,"E51"),sQuery(id+"F14.wireOp",EDGE,"E52"),sQuery(id+"F14.wireOp",EDGE,"E53")])]}),"instanceName":"1"});
            transform(context, id + "F18", {"entities" : qUnion([Q0]), "transformType" : TransformType.TRANSLATION_3D, "dx" : 0 * mm, "dy" : 0 * mm, "dz" : -10 * mm, "makeCopy" : true});
        }
        {
            var Q0;
            Q0=makeQuery(id+"F14.imprint","IMPRINT",FACE,{"disambiguationData":[TD([[makeQuery(id+"F14.imprint","IMPRINT",EDGE,{"derivedFrom":sQuery(id+"F14.wireOp",EDGE,"E59")}),-1.0]])]});
            extrude(context, id + "F19", {"entities" : qUnion([Q0]), "depth" : 2 * mm, "offsetDistance" : 25 * mm});
        }
        {
            var Q0;
            Q0=makeQuery(id+"F19.opExtrude","CAP_FACE",FACE,{"disambiguationData":[OSD([sQuery(id+"F14.wireOp",EDGE,"E59"),sQuery(id+"F14.wireOp",EDGE,"E60.MirrorCS"),sQuery(id+"F14.wireOp",EDGE,"E61"),sQuery(id+"F14.wireOp",EDGE,"E62")])],"isStart":false});
            var Q1;
            Q1=makeQuery(id+"F19.opExtrude","CAP_EDGE",EDGE,{"disambiguationData":[OSD([sQuery(id+"F14.wireOp",EDGE,"E59")])],"isStart":true});
            var Q2;
            Q2=makeQuery(id+"F19.opExtrude","CAP_EDGE",EDGE,{"disambiguationData":[OSD([sQuery(id+"F14.wireOp",EDGE,"E62")])],"isStart":true});
            fillet(context, id + "F20", {"entities" : qUnion([Q0, Q1, Q2]), "radius" : 1 * mm, "tangentPropagation" : true, "allowEdgeOverflow" : false});
        }
        {
            var Q0;
            Q0=makeQuery(id+"F2.opRevolve","SWEPT_EDGE",EDGE,{"disambiguationData":[OSD([sQuery(id+"F0.wireOp",EDGE,"E4"),sQuery(id+"F0.wireOp",EDGE,"uGP4i8PR-qrVT-5yK9-WrHV-lRQaqzL6runP")])]});
            var Q1;
            Q1=makeQuery(id+"F2.opRevolve","SWEPT_EDGE",EDGE,{"disambiguationData":[OSD([sQuery(id+"F0.wireOp",EDGE,"E3"),sQuery(id+"F0.wireOp",EDGE,"E4")])]});
            var Q2;
            Q2=makeQuery(id+"F2.opRevolve","SWEPT_EDGE",EDGE,{"disambiguationData":[OSD([sQuery(id+"F0.wireOp",EDGE,"BNsQ9w4D-RSQq-rLd6-vEkO-ORCSlvimwIOu"),sQuery(id+"F0.wireOp",EDGE,"tNqeK4Cf-ASuU-CWxC-Zfmx-HYztnxd8f7dT")])]});
            var Q3;
            Q3=makeQuery(id+"F2.opRevolve","SWEPT_EDGE",EDGE,{"disambiguationData":[OSD([sQuery(id+"F0.wireOp",EDGE,"uGP4i8PR-qrVT-5yK9-WrHV-lRQaqzL6runP"),sQuery(id+"F0.wireOp",EDGE,"BNsQ9w4D-RSQq-rLd6-vEkO-ORCSlvimwIOu")])]});
            fillet(context, id + "F21", {"entities" : qUnion([Q0, Q1, Q2, Q3]), "radius" : 1 * mm, "tangentPropagation" : true, "allowEdgeOverflow" : false});
        }
        {
            var Q0;
            Q0=qCreatedBy(makeId("Front.planeOp"),FACE);
            var sketch = newSketch(context, id + "F22", { "sketchPlane" : qUnion([Q0])});
            skLineSegment(sketch, "E65", {"start": v(-3.48, 1.15) * mm, "end": v(2.84, 0.58) * mm});
            skLineSegment(sketch, "E66", {"start": v(2.84, 0.58) * mm, "end": v(2.84, 2.16) * mm});
            skLineSegment(sketch, "E67", {"start": v(2.84, 2.16) * mm, "end": v(-3.48, 2.16) * mm});
            skLineSegment(sketch, "E68", {"start": v(-3.48, 1.15) * mm, "end": v(-3.48, 2.16) * mm});
            skLineSegment(sketch, "E69", {"start": v(1.92, 0) * mm, "end": v(1.92, 0.58) * mm});
            skLineSegment(sketch, "E70", {"start": v(1.92, 0.58) * mm, "end": v(-4.4, 1.15) * mm});
            skLineSegment(sketch, "E71", {"start": v(-4.4, 1.15) * mm, "end": v(-4.4, 0) * mm});
            skLineSegment(sketch, "E72", {"start": v(-4.4, 0) * mm, "end": v(1.92, 0) * mm});
            skSolve(sketch);
        }
        {
            var Q0;
            Q0=makeQuery(id+"F22.imprint","IMPRINT",FACE,{"disambiguationData":[TD([[makeQuery(id+"F22.imprint","IMPRINT",EDGE,{"derivedFrom":sQuery(id+"F22.wireOp",EDGE,"E65")}),1.0]])]});
            var Q1;
            Q1=makeQuery(id+"F22.imprint","IMPRINT",FACE,{"disambiguationData":[TD([[makeQuery(id+"F22.imprint","IMPRINT",EDGE,{"derivedFrom":sQuery(id+"F22.wireOp",EDGE,"E69")}),1.0]])]});
            var Q2;
            Q2=sQuery(id+"F22.wireOp",EDGE,"E67");
            var Q3;
            Q3=sQuery(id+"F22.wireOp",EDGE,"E68");
            var Q4;
            Q4=sQuery(id+"F22.wireOp",EDGE,"E65");
            var Q5;
            Q5=sQuery(id+"F22.wireOp",EDGE,"E66");
            extrude(context, id + "F23", {"entities" : qUnion([Q0, Q1]), "surfaceEntities" : qUnion([Q2, Q3, Q4, Q5]), "depth" : 1 * mm, "offsetDistance" : 25 * mm});
        }
        {
            var Q0;
            Q0=makeQuery(id+"F19.opExtrude","SWEPT_BODY",BODY,{"disambiguationData":[OSD([sQuery(id+"F14.wireOp",EDGE,"E59"),sQuery(id+"F14.wireOp",EDGE,"E60.MirrorCS"),sQuery(id+"F14.wireOp",EDGE,"E61"),sQuery(id+"F14.wireOp",EDGE,"E62")])]});
            transform(context, id + "F24", {"entities" : qUnion([Q0]), "transformType" : TransformType.TRANSLATION_3D, "dx" : 0 * mm, "dy" : 0 * mm, "dz" : -9.96 * mm, "makeCopy" : true});
        }
        {
            var Q0;
            Q0=makeQuery(id+"F14.imprint","IMPRINT",FACE,{"disambiguationData":[TD([[makeQuery(id+"F14.imprint","IMPRINT",EDGE,{"derivedFrom":sQuery(id+"F14.wireOp",EDGE,"E64.bottom")}),-1.0]])]});
            extrude(context, id + "F25", {"entities" : qUnion([Q0]), "depth" : 0.5 * mm, "offsetDistance" : 25 * mm});
        }
        {
            var Q0;
            Q0=makeQuery(id+"F25.opExtrude","SWEPT_BODY",BODY,{"disambiguationData":[OSD([sQuery(id+"F14.wireOp",EDGE,"E64.bottom"),sQuery(id+"F14.wireOp",EDGE,"E64.top"),sQuery(id+"F14.wireOp",EDGE,"E64.left"),sQuery(id+"F14.wireOp",EDGE,"E64.right")])]});
            transform(context, id + "F26", {"entities" : qUnion([Q0]), "transformType" : TransformType.TRANSLATION_3D, "dx" : 0 * mm, "dy" : -0.75 * mm, "dz" : -0.46 * mm, "makeCopy" : false});
        }
        {
            var Q0;
            Q0=makeQuery(id+"F25.opExtrude","SWEPT_FACE",FACE,{"disambiguationData":[OSD([sQuery(id+"F14.wireOp",EDGE,"E64.bottom")])]});
            var sketch = newSketch(context, id + "F27", { "sketchPlane" : qUnion([Q0])});
            skCircle(sketch, "E73", {"center": v(-81.54, -1.02) * mm, "radius": 2 * mm});
            skSolve(sketch);
        }
        {
            var Q0;
            Q0=makeQuery(id+"F27.imprint","IMPRINT",FACE,{"disambiguationData":[TD([[makeQuery(id+"F27.imprint","IMPRINT",EDGE,{"derivedFrom":sQuery(id+"F27.wireOp",EDGE,"E73")}),1.0]])]});
            extrude(context, id + "F28", {"entities" : qUnion([Q0]), "depth" : 1 * mm, "offsetDistance" : 25 * mm});
        }
        {
            var Q0;
            Q0=makeQuery(id+"F28.opExtrude","SWEPT_BODY",BODY,{"disambiguationData":[OSD([sQuery(id+"F14.wireOp",EDGE,"E64.bottom"),sQuery(id+"F14.wireOp",EDGE,"E64.left"),sQuery(id+"F14.wireOp",EDGE,"E64.right"),sQuery(id+"F27.wireOp",EDGE,"E73")])]});
            transform(context, id + "F29", {"entities" : qUnion([Q0]), "transformType" : TransformType.TRANSLATION_3D, "dx" : 0 * mm, "dy" : 0 * mm, "dz" : 1.43 * mm, "makeCopy" : false});
        }
        {
            var Q0;
            Q0=makeQuery(id+"F24.opPattern","COPY",BODY,{"derivedFrom":makeQuery(id+"F19.opExtrude","SWEPT_BODY",BODY,{"disambiguationData":[OSD([sQuery(id+"F14.wireOp",EDGE,"E59"),sQuery(id+"F14.wireOp",EDGE,"E60.MirrorCS"),sQuery(id+"F14.wireOp",EDGE,"E61"),sQuery(id+"F14.wireOp",EDGE,"E62")])]}),"instanceName":"1"});
            deleteBodies(context, id + "F30", {"entities" : qUnion([Q0])});
        }
        {
            var Q0;
            Q0=makeQuery(id+"F19.opExtrude","SWEPT_BODY",BODY,{"disambiguationData":[OSD([sQuery(id+"F14.wireOp",EDGE,"E59"),sQuery(id+"F14.wireOp",EDGE,"E60.MirrorCS"),sQuery(id+"F14.wireOp",EDGE,"E61"),sQuery(id+"F14.wireOp",EDGE,"E62")])]});
            transform(context, id + "F31", {"entities" : qUnion([Q0]), "transformType" : TransformType.TRANSLATION_3D, "dx" : 0 * mm, "dy" : 0 * mm, "dz" : -11.8 * mm, "makeCopy" : true});
        }
        {
            var Q0;
            Q0=makeQuery(id+"F31.opPattern","COPY",BODY,{"derivedFrom":makeQuery(id+"F19.opExtrude","SWEPT_BODY",BODY,{"disambiguationData":[OSD([sQuery(id+"F14.wireOp",EDGE,"E59"),sQuery(id+"F14.wireOp",EDGE,"E60.MirrorCS"),sQuery(id+"F14.wireOp",EDGE,"E61"),sQuery(id+"F14.wireOp",EDGE,"E62")])]}),"instanceName":"1"});
            transform(context, id + "F32", {"entities" : qUnion([Q0]), "transformType" : TransformType.TRANSLATION_3D, "dx" : 0 * mm, "dy" : 0 * mm, "dz" : 0 * mm, "makeCopy" : true});
        }
        {
            var Q0;
            Q0=makeQuery(id+"F32.opPattern","COPY",BODY,{"derivedFrom":makeQuery(id+"F31.opPattern","COPY",BODY,{"derivedFrom":makeQuery(id+"F19.opExtrude","SWEPT_BODY",BODY,{"disambiguationData":[OSD([sQuery(id+"F14.wireOp",EDGE,"E59"),sQuery(id+"F14.wireOp",EDGE,"E60.MirrorCS"),sQuery(id+"F14.wireOp",EDGE,"E61"),sQuery(id+"F14.wireOp",EDGE,"E62")])]}),"instanceName":"1"}),"instanceName":"1"});
            transform(context, id + "F33", {"entities" : qUnion([Q0]), "transformType" : TransformType.TRANSLATION_3D, "dx" : 0 * mm, "dy" : 0 * mm, "dz" : -11.72 * mm, "makeCopy" : true});
        }
    });
